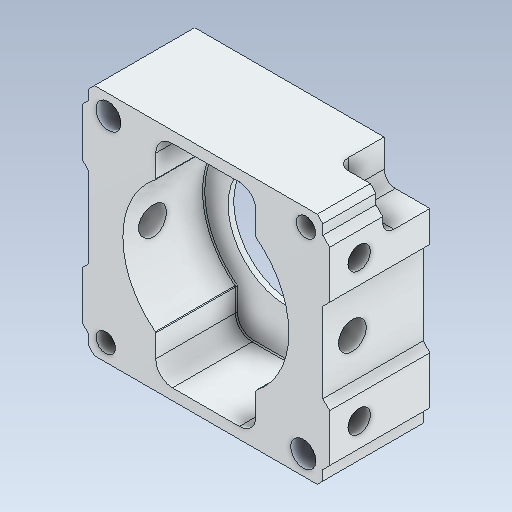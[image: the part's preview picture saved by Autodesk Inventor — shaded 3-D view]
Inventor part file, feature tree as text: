
AUTODESK INVENTOR PART (.ipt)
format: ipt  version: 2020 (Build 240168000, 168)  size: 270,848 bytes
history: native  units: in
note: dims shown in document units (in); Inventor stores cm internally (conversion verified against a paired STEP export)
features: chamfer x1
ambient origin geometry x8: Origin, YZ Plane, XZ Plane, XY Plane, X Axis, Y Axis, Z Axis, Center Point
bodies: Solid1 (feature_tree)
feature tree (1):
  chamfer  "Chamfer4"  [1 undecoded]
note: 1 required parameter value undecoded (feature->parameter linkage not recoverable at this tier; creation-order binding heuristic only, values carry confidence <= 0.55)
